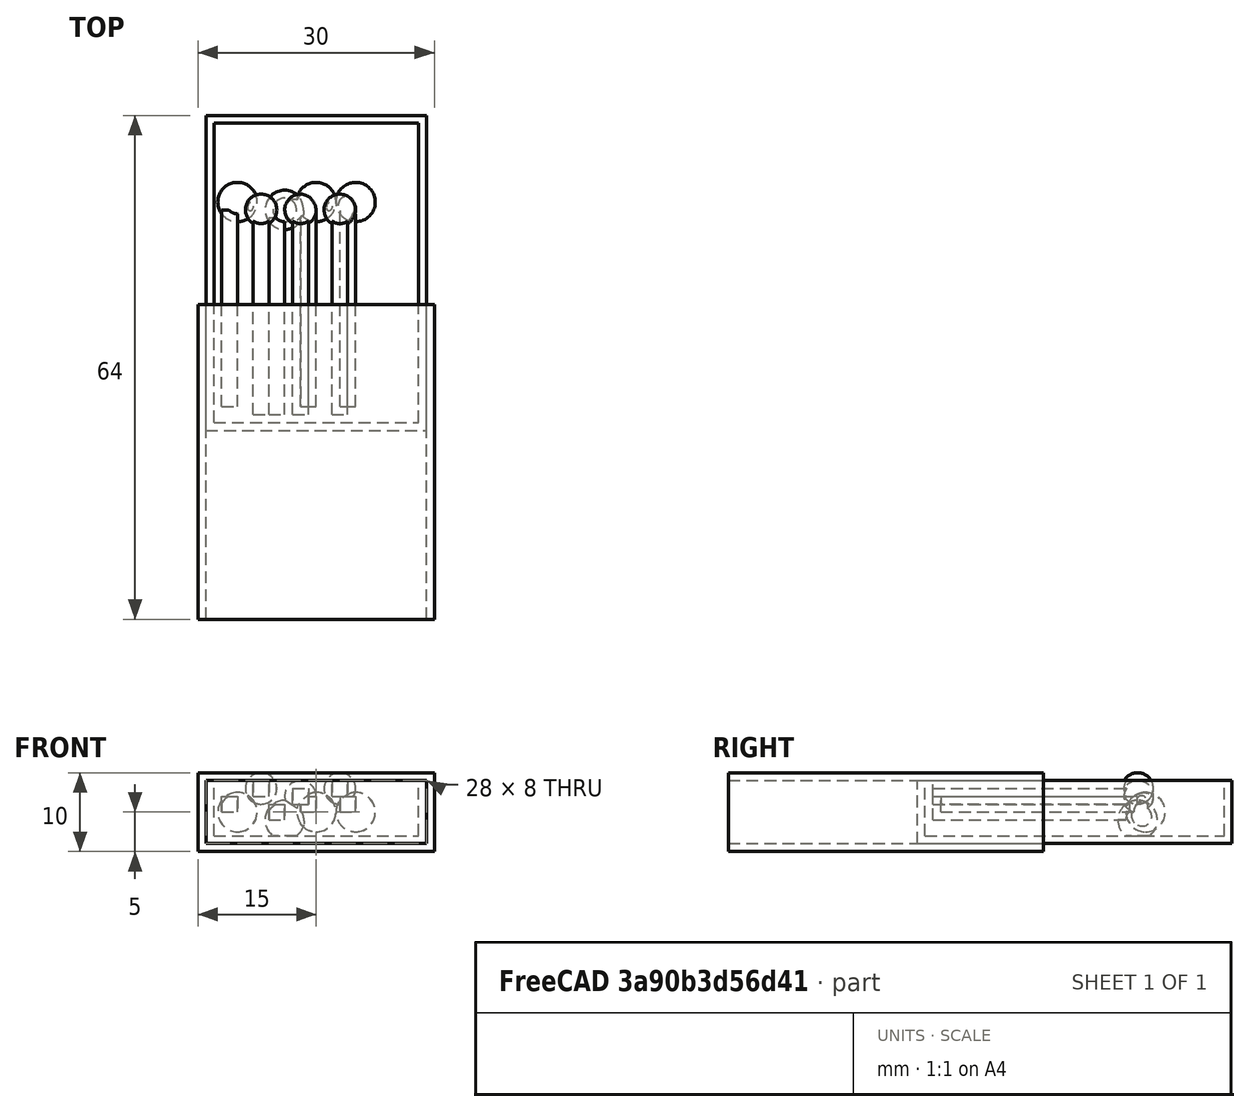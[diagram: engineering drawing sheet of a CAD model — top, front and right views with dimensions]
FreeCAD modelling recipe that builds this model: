
FCSTD DOCUMENT  (FreeCAD 0.18R4 (GitTag))
Label: g
License: All rights reserved
LicenseURL: http://en.wikipedia.org/wiki/All_rights_reserved
objects: Part::Box×11, Part::MultiFuse×9, Part::Sphere×7, Part::Cut×2
note: 29 computed .brp shape members not serialized (recipe doc carries the construction recipe); baked Part::Feature solids carry a one-line shape summary decoded from their .brp

FEATURE [Part::Box] Box  label="Куб"
  AttacherType = Attacher::AttachEngine3D
  Height = 10
  Length = 30
  Placement = pos=(0,1,0) rot=(0,0,1;0rad)
  Width = 40
FEATURE [Part::Box] Box001  label="Куб001"
  AttacherType = Attacher::AttachEngine3D
  Height = 8
  Length = 28
  Placement = pos=(1,1,1) rot=(0,0,1;0rad)
  Width = 40
FEATURE [Part::Box] Box002  label="Куб002"
  AttacherType = Attacher::AttachEngine3D
  Height = 8
  Length = 28
  Placement = pos=(1,1,1) rot=(0,0,1;0rad)
  Width = 40
FEATURE [Part::Cut] Cut
  Base = -> Box
  Tool = -> Box001
FEATURE [Part::Box] Box003  label="Куб003"
  AttacherType = Attacher::AttachEngine3D
  Height = 7
  Length = 26
  Placement = pos=(2,2,2) rot=(0,0,1;0rad)
  Width = 38
FEATURE [Part::Cut] Cut001
  Base = -> Box002
  Placement = pos=(0,25,0) rot=(0,0,1;0rad)
  Tool = -> Box003
FEATURE [Part::Box] Box004  label="Куб004"
  AttacherType = Attacher::AttachEngine3D
  Height = 2
  Length = 2
  Placement = pos=(3,28,2) rot=(0,0,1;0rad)
  Width = 25
FEATURE [Part::Sphere] Sphere  label="Сфера"
  Angle1 = -90
  Angle2 = 90
  Angle3 = 360
  AttacherType = Attacher::AttachEngine3D
  Placement = pos=(5,54,2) rot=(0,0,1;0rad)
  Radius = 2.5
FEATURE [Part::MultiFuse] Fusion
  Placement = pos=(0,1,3) rot=(0,0,1;0rad)
  Shapes = -> [Box004,Sphere]
FEATURE [Part::MultiFuse] Fusion004
  Placement = pos=(0,34,0) rot=(0,0,1;0rad)
  Shapes = -> [Cut001,Fusion]
FEATURE [Part::Box] Box005  label="Куб005"
  AttacherType = Attacher::AttachEngine3D
  Height = 2
  Length = 2
  Placement = pos=(3,28,2) rot=(0,0,1;0rad)
  Width = 25
FEATURE [Part::Sphere] Sphere001  label="Сфера001"
  Angle1 = -90
  Angle2 = 90
  Angle3 = 360
  AttacherType = Attacher::AttachEngine3D
  Placement = pos=(5,54,2) rot=(0,0,1;0rad)
  Radius = 2.5
FEATURE [Part::MultiFuse] Fusion005
  Placement = pos=(6,34,2) rot=(0,0,1;0rad)
  Shapes = -> [Box005,Sphere001]
FEATURE [Part::Box] Box006  label="Куб006"
  AttacherType = Attacher::AttachEngine3D
  Height = 2
  Length = 2
  Placement = pos=(3,28,2) rot=(0,0,1;0rad)
  Width = 25
FEATURE [Part::Sphere] Sphere002  label="Сфера002"
  Angle1 = -90
  Angle2 = 90
  Angle3 = 360
  AttacherType = Attacher::AttachEngine3D
  Placement = pos=(5,54,2) rot=(0,0,1;0rad)
  Radius = 2.5
FEATURE [Part::MultiFuse] Fusion006
  Placement = pos=(10,35,3) rot=(0,0,1;0rad)
  Shapes = -> [Box006,Sphere002]
FEATURE [Part::Box] Box007  label="Куб007"
  AttacherType = Attacher::AttachEngine3D
  Height = 2
  Length = 2
  Placement = pos=(3,28,2) rot=(0,0,1;0rad)
  Width = 25
FEATURE [Part::Sphere] Sphere003  label="Сфера003"
  Angle1 = -90
  Angle2 = 90
  Angle3 = 360
  AttacherType = Attacher::AttachEngine3D
  Placement = pos=(5,54,2) rot=(0,0,1;0rad)
  Radius = 2.5
FEATURE [Part::MultiFuse] Fusion007
  Placement = pos=(15,35,3) rot=(0,0,1;0rad)
  Shapes = -> [Box007,Sphere003]
FEATURE [Part::Box] Box008  label="Куб008"
  AttacherType = Attacher::AttachEngine3D
  Height = 2
  Length = 2
  Placement = pos=(3,28,2) rot=(0,0,1;0rad)
  Width = 25
FEATURE [Part::Sphere] Sphere004  label="Сфера004"
  Angle1 = -90
  Angle2 = 90
  Angle3 = 360
  AttacherType = Attacher::AttachEngine3D
  Placement = pos=(4,54,3) rot=(0,0,1;0rad)
  Radius = 2
FEATURE [Part::MultiFuse] Fusion008
  Placement = pos=(9,34,4) rot=(0,0,1;0rad)
  Shapes = -> [Box008,Sphere004]
FEATURE [Part::Sphere] Sphere005  label="Сфера005"
  Angle1 = -90
  Angle2 = 90
  Angle3 = 360
  AttacherType = Attacher::AttachEngine3D
  Placement = pos=(4,54,3) rot=(0,0,1;0rad)
  Radius = 2
FEATURE [Part::Box] Box009  label="Куб009"
  AttacherType = Attacher::AttachEngine3D
  Height = 2
  Length = 2
  Placement = pos=(3,28,2) rot=(0,0,1;0rad)
  Width = 25
FEATURE [Part::MultiFuse] Fusion009
  Placement = pos=(4,34,5) rot=(0,0,1;0rad)
  Shapes = -> [Box009,Sphere005]
FEATURE [Part::Sphere] Sphere006  label="Сфера006"
  Angle1 = -90
  Angle2 = 90
  Angle3 = 360
  AttacherType = Attacher::AttachEngine3D
  Placement = pos=(4,54,3) rot=(0,0,1;0rad)
  Radius = 2
FEATURE [Part::Box] Box010  label="Куб010"
  AttacherType = Attacher::AttachEngine3D
  Height = 2
  Length = 2
  Placement = pos=(3,28,2) rot=(0,0,1;0rad)
  Width = 25
FEATURE [Part::MultiFuse] Fusion010
  Placement = pos=(14,34,5) rot=(0,0,1;0rad)
  Shapes = -> [Box010,Sphere006]
FEATURE [Part::MultiFuse] Fusion011
  Placement = pos=(0,-35,0) rot=(0,0,1;0rad)
  Shapes = -> [Fusion004,Fusion005,Fusion006,Fusion007,Fusion008,Fusion010,Fusion009]
